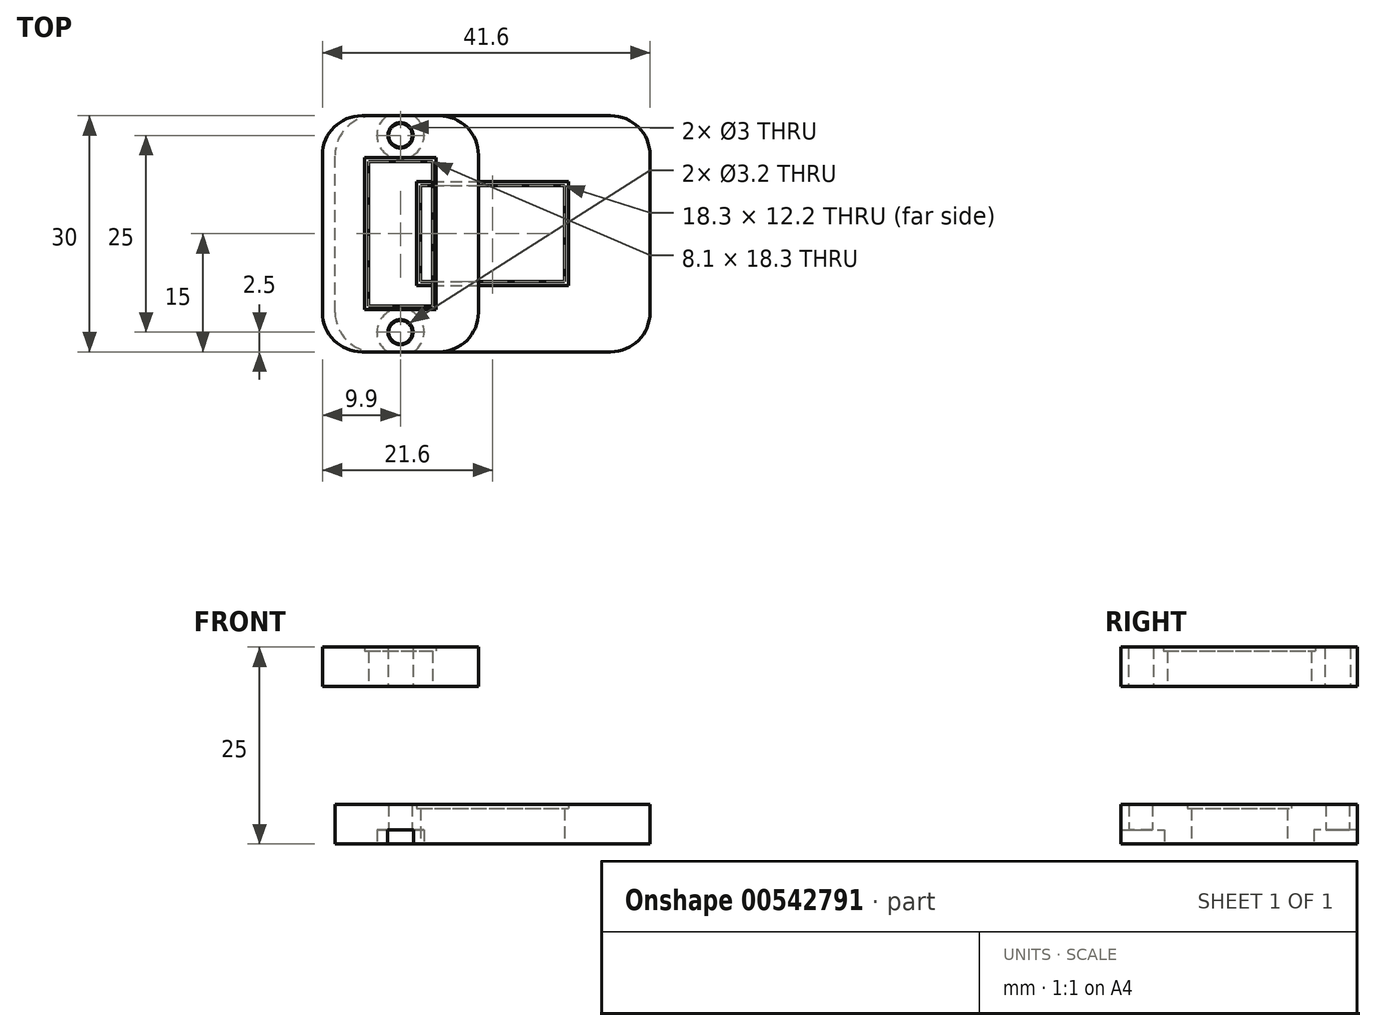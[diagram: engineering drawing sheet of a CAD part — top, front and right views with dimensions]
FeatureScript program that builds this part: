
annotation { "Feature Type Name" : "Feature", "Feature Type Description" : "" }
export const myFeature = defineFeature(function(context is Context, id is Id, definition is map)
    precondition{}
    {
        {
            var Q0;
            Q0=qCreatedBy(makeId("Top.planeOp"),FACE);
            var sketch = newSketch(context, id + "F0", { "sketchPlane" : qUnion([Q0])});
            skLineSegment(sketch, "E0.bottom", {"start": v(-9.65, -6.6) * mm, "end": v(9.65, -6.6) * mm});
            skLineSegment(sketch, "E0.top", {"start": v(-9.65, 6.6) * mm, "end": v(9.65, 6.6) * mm});
            skLineSegment(sketch, "E0.left", {"start": v(-9.65, -6.6) * mm, "end": v(-9.65, 6.6) * mm});
            skLineSegment(sketch, "E0.right", {"start": v(9.65, -6.6) * mm, "end": v(9.65, 6.6) * mm});
            skPoint(sketch, "E0.middle", {"position": v(0, 0) * mm});
            skLineSegment(sketch, "E1.bottom", {"start": v(-20, -15) * mm, "end": v(20, -15) * mm});
            skLineSegment(sketch, "E1.top", {"start": v(-20, 15) * mm, "end": v(20, 15) * mm});
            skLineSegment(sketch, "E1.left", {"start": v(-20, -15) * mm, "end": v(-20, 15) * mm});
            skLineSegment(sketch, "E1.right", {"start": v(20, -15) * mm, "end": v(20, 15) * mm});
            skLineSegment(sketch, "E2.bottom", {"start": v(-16.25, -9.65) * mm, "end": v(-7.15, -9.65) * mm});
            skLineSegment(sketch, "E2.top", {"start": v(-16.25, 9.65) * mm, "end": v(-7.15, 9.65) * mm});
            skLineSegment(sketch, "E2.left", {"start": v(-16.25, -9.65) * mm, "end": v(-16.25, 9.65) * mm});
            skLineSegment(sketch, "E2.right", {"start": v(-7.15, -9.65) * mm, "end": v(-7.15, 9.65) * mm});
            skPoint(sketch, "E2.middle", {"position": v(-11.7, 0) * mm});
            skLineSegment(sketch, "E3.0", {"start": v(-9.15, 6.1) * mm, "end": v(9.15, 6.1) * mm});
            skLineSegment(sketch, "E3.1", {"start": v(-9.15, -6.1) * mm, "end": v(-9.15, 6.1) * mm});
            skLineSegment(sketch, "E3.2", {"start": v(-9.15, -6.1) * mm, "end": v(9.15, -6.1) * mm});
            skLineSegment(sketch, "E3.3", {"start": v(9.15, -6.1) * mm, "end": v(9.15, 6.1) * mm});
            skLineSegment(sketch, "E4.0", {"start": v(-7.65, -9.15) * mm, "end": v(-7.65, 9.15) * mm});
            skLineSegment(sketch, "E4.1", {"start": v(-15.75, -9.15) * mm, "end": v(-7.65, -9.15) * mm});
            skLineSegment(sketch, "E4.2", {"start": v(-15.75, -9.15) * mm, "end": v(-15.75, 9.15) * mm});
            skLineSegment(sketch, "E4.3", {"start": v(-15.75, 9.15) * mm, "end": v(-7.65, 9.15) * mm});
            skLineSegment(sketch, "E5.0", {"start": v(-1.8, -15) * mm, "end": v(-1.8, 15) * mm});
            skLineSegment(sketch, "E5.1", {"start": v(-21.6, -15) * mm, "end": v(-1.8, -15) * mm});
            skLineSegment(sketch, "E5.2", {"start": v(-21.6, -15) * mm, "end": v(-21.6, 15) * mm});
            skLineSegment(sketch, "E5.3", {"start": v(-21.6, 15) * mm, "end": v(-1.8, 15) * mm});
            skLineSegment(sketch, "E6", {"start": v(-11.7, -15.97) * mm, "end": v(-11.7, 16.71) * mm, "construction": true});
            skPoint(sketch, "E7", {"position": v(-11.7, -12.5) * mm});
            skPoint(sketch, "E8.MirrorP", {"position": v(-11.7, 12.5) * mm});
            skSolve(sketch);
        }
        {
            var Q0;
            {var subQ2=sQuery(id+"F0.wireOp",EDGE,"E0.right");Q0=makeQuery(id+"F0.imprint","IMPRINT",FACE,{"disambiguationData":[TD([[makeQuery(id+"F0.imprint","IMPRINT",EDGE,{"derivedFrom":subQ2}),-1.0]])]});}
            var Q1;
            {var subQ0=sQuery(id+"F0.wireOp",EDGE,"E0.left");Q1=makeQuery(id+"F0.imprint","IMPRINT",FACE,{"disambiguationData":[TD([[makeQuery(id+"F0.imprint","IMPRINT",EDGE,{"derivedFrom":subQ0}),1.0]])]});}
            var Q2;
            {var subQ10=sQuery(id+"F0.wireOp",EDGE,"E2.bottom");Q2=makeQuery(id+"F0.imprint","IMPRINT",FACE,{"disambiguationData":[TD([[makeQuery(id+"F0.imprint","IMPRINT",EDGE,{"derivedFrom":subQ10}),1.0]])]});}
            var Q3;
            {var subQ14=sQuery(id+"F0.wireOp",EDGE,"E1.left");Q3=makeQuery(id+"F0.imprint","IMPRINT",FACE,{"disambiguationData":[TD([[makeQuery(id+"F0.imprint","IMPRINT",EDGE,{"derivedFrom":subQ14}),-1.0]])]});}
            extrude(context, id + "F1", {"entities" : qUnion([Q0, Q1, Q2, Q3]), "depth" : 5 * mm, "offsetDistance" : 25 * mm});
        }
        {
            var Q0;
            {var subQ0=sQuery(id+"F0.wireOp",EDGE,"E0.left");Q0=makeQuery(id+"F0.imprint","IMPRINT",FACE,{"disambiguationData":[TD([[makeQuery(id+"F0.imprint","IMPRINT",EDGE,{"derivedFrom":subQ0}),-1.0]])]});}
            var Q1;
            {var subQ0=sQuery(id+"F0.wireOp",EDGE,"E4.0");var subQ1=sQuery(id+"F0.wireOp",EDGE,"E0.top");var subQ2=makeQuery(id+"F0.imprint","INTERSECT",VERTEX,{"derivedFrom":[subQ1,subQ0]});Q1=makeQuery(id+"F0.imprint","IMPRINT",FACE,{"disambiguationData":[TD([[makeQuery(id+"F0.imprint","IMPRINT",EDGE,{"disambiguationData":[TD([[subQ2,-1.0]])],"derivedFrom":subQ1}),-1.0]])]});}
            var Q2;
            {var subQ5=sQuery(id+"F0.wireOp",EDGE,"E0.right");Q2=makeQuery(id+"F0.imprint","IMPRINT",FACE,{"disambiguationData":[TD([[makeQuery(id+"F0.imprint","IMPRINT",EDGE,{"derivedFrom":subQ5}),1.0]])]});}
            var Q3;
            {var subQ0=sQuery(id+"F0.wireOp",EDGE,"E4.0");var subQ1=sQuery(id+"F0.wireOp",EDGE,"E0.bottom");var subQ2=makeQuery(id+"F0.imprint","INTERSECT",VERTEX,{"derivedFrom":[subQ1,subQ0]});Q3=makeQuery(id+"F0.imprint","IMPRINT",FACE,{"disambiguationData":[TD([[makeQuery(id+"F0.imprint","IMPRINT",EDGE,{"disambiguationData":[TD([[subQ2,-1.0]])],"derivedFrom":subQ1}),1.0]])]});}
            var Q4;
            {var subQ0=sQuery(id+"F0.wireOp",EDGE,"E2.right");var subQ1=sQuery(id+"F0.wireOp",EDGE,"E0.bottom");var subQ2=makeQuery(id+"F0.imprint","INTERSECT",VERTEX,{"derivedFrom":[subQ1,subQ0]});Q4=makeQuery(id+"F0.imprint","IMPRINT",FACE,{"disambiguationData":[TD([[makeQuery(id+"F0.imprint","IMPRINT",EDGE,{"disambiguationData":[TD([[subQ2,-1.0]])],"derivedFrom":subQ1}),1.0]])]});}
            var Q5;
            {var subQ0=sQuery(id+"F0.wireOp",EDGE,"E2.right");var subQ1=sQuery(id+"F0.wireOp",EDGE,"E0.top");var subQ2=makeQuery(id+"F0.imprint","INTERSECT",VERTEX,{"derivedFrom":[subQ1,subQ0]});Q5=makeQuery(id+"F0.imprint","IMPRINT",FACE,{"disambiguationData":[TD([[makeQuery(id+"F0.imprint","IMPRINT",EDGE,{"disambiguationData":[TD([[subQ2,-1.0]])],"derivedFrom":subQ1}),-1.0]])]});}
            extrude(context, id + "F2", {"entities" : qUnion([Q0, Q1, Q2, Q3, Q4, Q5]), "operationType" : NewBodyOperationType.ADD, "depth" : 4.5 * mm, "offsetDistance" : 25 * mm});
        }
        {
            var Q0;
            Q0=makeQuery(id+"F1.opExtrude","SWEPT_EDGE",EDGE,{"disambiguationData":[OSD([sQuery(id+"F0.wireOp",EDGE,"E1.bottom"),sQuery(id+"F0.wireOp",EDGE,"E1.left")])]});
            var Q1;
            Q1=makeQuery(id+"F1.opExtrude","SWEPT_EDGE",EDGE,{"disambiguationData":[OSD([sQuery(id+"F0.wireOp",EDGE,"E1.bottom"),sQuery(id+"F0.wireOp",EDGE,"E1.right")])]});
            var Q2;
            Q2=makeQuery(id+"F1.opExtrude","SWEPT_EDGE",EDGE,{"disambiguationData":[OSD([sQuery(id+"F0.wireOp",EDGE,"E1.top"),sQuery(id+"F0.wireOp",EDGE,"E1.left")])]});
            var Q3;
            Q3=makeQuery(id+"F1.opExtrude","SWEPT_EDGE",EDGE,{"disambiguationData":[OSD([sQuery(id+"F0.wireOp",EDGE,"E1.top"),sQuery(id+"F0.wireOp",EDGE,"E1.right")])]});
            fillet(context, id + "F3", {"entities" : qUnion([Q0, Q1, Q2, Q3]), "radius" : 5 * mm, "tangentPropagation" : true, "allowEdgeOverflow" : false});
        }
        {
            var Q0;
            Q0=sQuery(id+"F0.wireOp",VERTEX,"E7");
            var Q1;
            Q1=sQuery(id+"F0.wireOp",VERTEX,"E8.MirrorP");
            var Q2;
            Q2=makeQuery(id+"F1.opExtrude","SWEPT_BODY",BODY,{"disambiguationData":[OSD([sQuery(id+"F0.wireOp",EDGE,"E0.bottom"),sQuery(id+"F0.wireOp",EDGE,"E0.top"),sQuery(id+"F0.wireOp",EDGE,"E0.left"),sQuery(id+"F0.wireOp",EDGE,"E0.right"),sQuery(id+"F0.wireOp",EDGE,"E1.bottom"),sQuery(id+"F0.wireOp",EDGE,"E1.top"),sQuery(id+"F0.wireOp",EDGE,"E1.left"),sQuery(id+"F0.wireOp",EDGE,"E1.right"),sQuery(id+"F0.wireOp",EDGE,"E5.1"),sQuery(id+"F0.wireOp",EDGE,"E5.3")])]});
            hole(context, id + "F4", {"style" : HoleStyle.C_BORE, "endStyle" : HoleEndStyle.BLIND, "oppositeDirection" : true, "holeDiameter" : 3 * mm, "cBoreDiameter" : 6 * mm, "cBoreDepth" : (0.6 * 3) * mm, "holeDepth" : 10 * mm, "isTappedThrough" : true, "tappedDepth" : 12 * mm, "tapClearance" : 3, "locations" : qUnion([Q0, Q1]), "scope" : qUnion([Q2])});
        }
        {
            var Q0;
            Q0=makeQuery(id+"F1.opExtrude","CAP_FACE",FACE,{"disambiguationData":[OSD([sQuery(id+"F0.wireOp",EDGE,"E0.bottom"),sQuery(id+"F0.wireOp",EDGE,"E0.top"),sQuery(id+"F0.wireOp",EDGE,"E0.left"),sQuery(id+"F0.wireOp",EDGE,"E0.right"),sQuery(id+"F0.wireOp",EDGE,"E1.bottom"),sQuery(id+"F0.wireOp",EDGE,"E1.top"),sQuery(id+"F0.wireOp",EDGE,"E1.left"),sQuery(id+"F0.wireOp",EDGE,"E1.right"),sQuery(id+"F0.wireOp",EDGE,"E5.1"),sQuery(id+"F0.wireOp",EDGE,"E5.3")])],"isStart":false});
            cPlane(context, id + "F5", {"entities" : qUnion([Q0]), "cplaneType" : CPlaneType.OFFSET, "offset" : 15 * mm, "width" : 150 * mm, "height" : 150 * mm});
        }
        {
            var Q0;
            Q0=qCreatedBy(id+"F5.planeOp",FACE);
            var sketch = newSketch(context, id + "F6", { "sketchPlane" : qUnion([Q0])});
            skLineSegment(sketch, "E9.0", {"start": v(-1.8, -15) * mm, "end": v(-1.8, 15) * mm});
            skLineSegment(sketch, "E9.1", {"start": v(-21.6, -15) * mm, "end": v(-1.8, -15) * mm});
            skLineSegment(sketch, "E9.2", {"start": v(-21.6, -15) * mm, "end": v(-21.6, 15) * mm});
            skLineSegment(sketch, "E9.3", {"start": v(-21.6, 15) * mm, "end": v(-1.8, 15) * mm});
            skPoint(sketch, "E9.4", {"position": v(-11.7, 12.5) * mm});
            skLineSegment(sketch, "E9.5", {"start": v(-16.25, 9.65) * mm, "end": v(-7.15, 9.65) * mm});
            skLineSegment(sketch, "E9.6", {"start": v(-16.25, -9.65) * mm, "end": v(-16.25, 9.65) * mm});
            skLineSegment(sketch, "E9.7", {"start": v(-7.15, -9.65) * mm, "end": v(-7.15, 9.65) * mm});
            skLineSegment(sketch, "E9.8", {"start": v(-16.25, -9.65) * mm, "end": v(-7.15, -9.65) * mm});
            skLineSegment(sketch, "E9.9", {"start": v(-15.75, -9.15) * mm, "end": v(-7.65, -9.15) * mm});
            skLineSegment(sketch, "E9.10", {"start": v(-15.75, -9.15) * mm, "end": v(-15.75, 9.15) * mm});
            skLineSegment(sketch, "E9.11", {"start": v(-15.75, 9.15) * mm, "end": v(-7.65, 9.15) * mm});
            skLineSegment(sketch, "E9.12", {"start": v(-7.65, -9.15) * mm, "end": v(-7.65, 9.15) * mm});
            skPoint(sketch, "E9.13", {"position": v(-11.7, -12.5) * mm});
            skSolve(sketch);
        }
        {
            var Q0;
            Q0=makeQuery(id+"F6.imprint","IMPRINT",FACE,{"disambiguationData":[TD([[makeQuery(id+"F6.imprint","IMPRINT",EDGE,{"derivedFrom":sQuery(id+"F6.wireOp",EDGE,"E9.0")}),1.0]])]});
            extrude(context, id + "F7", {"entities" : qUnion([Q0]), "depth" : 5 * mm, "offsetDistance" : 25 * mm});
        }
        {
            var Q0;
            Q0=makeQuery(id+"F6.imprint","IMPRINT",FACE,{"disambiguationData":[TD([[makeQuery(id+"F6.imprint","IMPRINT",EDGE,{"derivedFrom":sQuery(id+"F6.wireOp",EDGE,"E9.5")}),-1.0]])]});
            extrude(context, id + "F8", {"entities" : qUnion([Q0]), "operationType" : NewBodyOperationType.ADD, "depth" : 4.5 * mm, "offsetDistance" : 25 * mm});
        }
        {
            var Q0;
            Q0=makeQuery(id+"F7.opExtrude","SWEPT_EDGE",EDGE,{"disambiguationData":[OSD([sQuery(id+"F6.wireOp",EDGE,"E9.0"),sQuery(id+"F6.wireOp",EDGE,"E9.3")])]});
            var Q1;
            Q1=makeQuery(id+"F7.opExtrude","SWEPT_EDGE",EDGE,{"disambiguationData":[OSD([sQuery(id+"F6.wireOp",EDGE,"E9.2"),sQuery(id+"F6.wireOp",EDGE,"E9.3")])]});
            var Q2;
            Q2=makeQuery(id+"F7.opExtrude","SWEPT_EDGE",EDGE,{"disambiguationData":[OSD([sQuery(id+"F6.wireOp",EDGE,"E9.1"),sQuery(id+"F6.wireOp",EDGE,"E9.2")])]});
            var Q3;
            Q3=makeQuery(id+"F7.opExtrude","SWEPT_EDGE",EDGE,{"disambiguationData":[OSD([sQuery(id+"F6.wireOp",EDGE,"E9.0"),sQuery(id+"F6.wireOp",EDGE,"E9.1")])]});
            fillet(context, id + "F9", {"entities" : qUnion([Q0, Q1, Q2, Q3]), "radius" : 5 * mm, "tangentPropagation" : true, "allowEdgeOverflow" : false});
        }
        {
            var Q0;
            Q0=sQuery(id+"F6.wireOp",VERTEX,"E9.13");
            var Q1;
            Q1=sQuery(id+"F6.wireOp",VERTEX,"E9.4");
            var Q2;
            Q2=makeQuery(id+"F7.opExtrude","SWEPT_BODY",BODY,{"disambiguationData":[OSD([sQuery(id+"F6.wireOp",EDGE,"E9.0"),sQuery(id+"F6.wireOp",EDGE,"E9.1"),sQuery(id+"F6.wireOp",EDGE,"E9.2"),sQuery(id+"F6.wireOp",EDGE,"E9.3"),sQuery(id+"F6.wireOp",EDGE,"E9.5"),sQuery(id+"F6.wireOp",EDGE,"E9.6"),sQuery(id+"F6.wireOp",EDGE,"E9.7"),sQuery(id+"F6.wireOp",EDGE,"E9.8")])]});
            hole(context, id + "F10", {"style" : HoleStyle.SIMPLE, "endStyle" : HoleEndStyle.BLIND, "oppositeDirection" : true, "holeDiameter" : 3.2 * mm, "holeDepth" : 10 * mm, "isTappedThrough" : true, "tappedDepth" : 12 * mm, "tapClearance" : 3, "locations" : qUnion([Q0, Q1]), "scope" : qUnion([Q2])});
        }
    });
